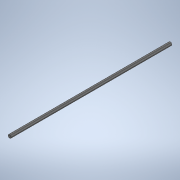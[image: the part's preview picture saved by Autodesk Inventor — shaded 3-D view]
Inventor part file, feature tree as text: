
AUTODESK INVENTOR PART (.ipt)
format: ipt  version: 2020 (Build 240168000, 168)  size: 137,216 bytes
history: native  units: in
note: dims shown in document units (in); Inventor stores cm internally (conversion verified against a paired STEP export)
features: plane x1, extrude x1, sketch x1, other x1
ambient origin geometry x8: Origin, YZ Plane, XZ Plane, XY Plane, X Axis, Y Axis, Z Axis, Center Point
bodies: Solid1 (feature_tree)
feature tree (4):
  plane  "Work Plane1"
  extrude  "Extrusion1"  Depth=1.0in
  sketch  "Sketch1"  dims[d0=-27.0in d1=1.0in d2=1.0in d3=2.0in d4=2.0in d5=27.0in d6=0.0in]
  other  "Cut-Extrude2"
